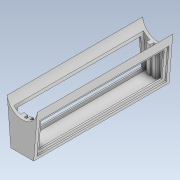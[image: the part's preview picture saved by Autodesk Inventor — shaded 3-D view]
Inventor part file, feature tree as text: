
AUTODESK INVENTOR PART (.ipt)
format: ipt  version: 2021 (Build 250183000, 183)  size: 172,544 bytes
history: native  units: in
note: dims shown in document units (in); Inventor stores cm internally (conversion verified against a paired STEP export)
features: extrude x5, sketch x5, mirror x2, projected_geometry x2, shell x1, plane x1
ambient origin geometry x8: Origin, YZ Plane, XZ Plane, XY Plane, X Axis, Y Axis, Z Axis, Center Point
bodies: Solid1 (feature_tree)
feature tree (16):
  extrude  "Extrusion1"  Depth=1.5in
  shell  "Shell1"  Thickness=0.3804in
  sketch  "Sketch2"  dims[d3=0.3804in d4=4.5in d5=0.0in]
  extrude  "Extrusion2"  Depth=4.5in TaperAngle=0.0deg
  extrude  "Extrusion3"  Depth=0.05in TaperAngle=0.0deg
  mirror  "Mirror1"
  extrude  "Extrusion4"  Depth=0.05in TaperAngle=0.0deg
  plane  "Work Plane1"
  mirror  "Mirror2"
  extrude  "Extrusion6"  Depth=0.12in
  sketch  "Sketch1"  dims[d0=1.0in d1=1.5in d2=0.3804in]
  projected_geometry  "Projected Loop1"
  sketch  "Sketch3"  dims[d6=0.1in d7=0.05in d8=0.0in]
  projected_geometry  "Projected Loop2"
  sketch  "Sketch4"  dims[d9=0.1in d10=0.05in d11=0.0in]
  sketch  "Sketch6"  dims[d12=0.035in d13=0.12in d14=0.12in d15=1.05in d16=0.0in d19=-2.25in d20=12.0in d21=0.0in d22=0.5in d23=0.0344in]
